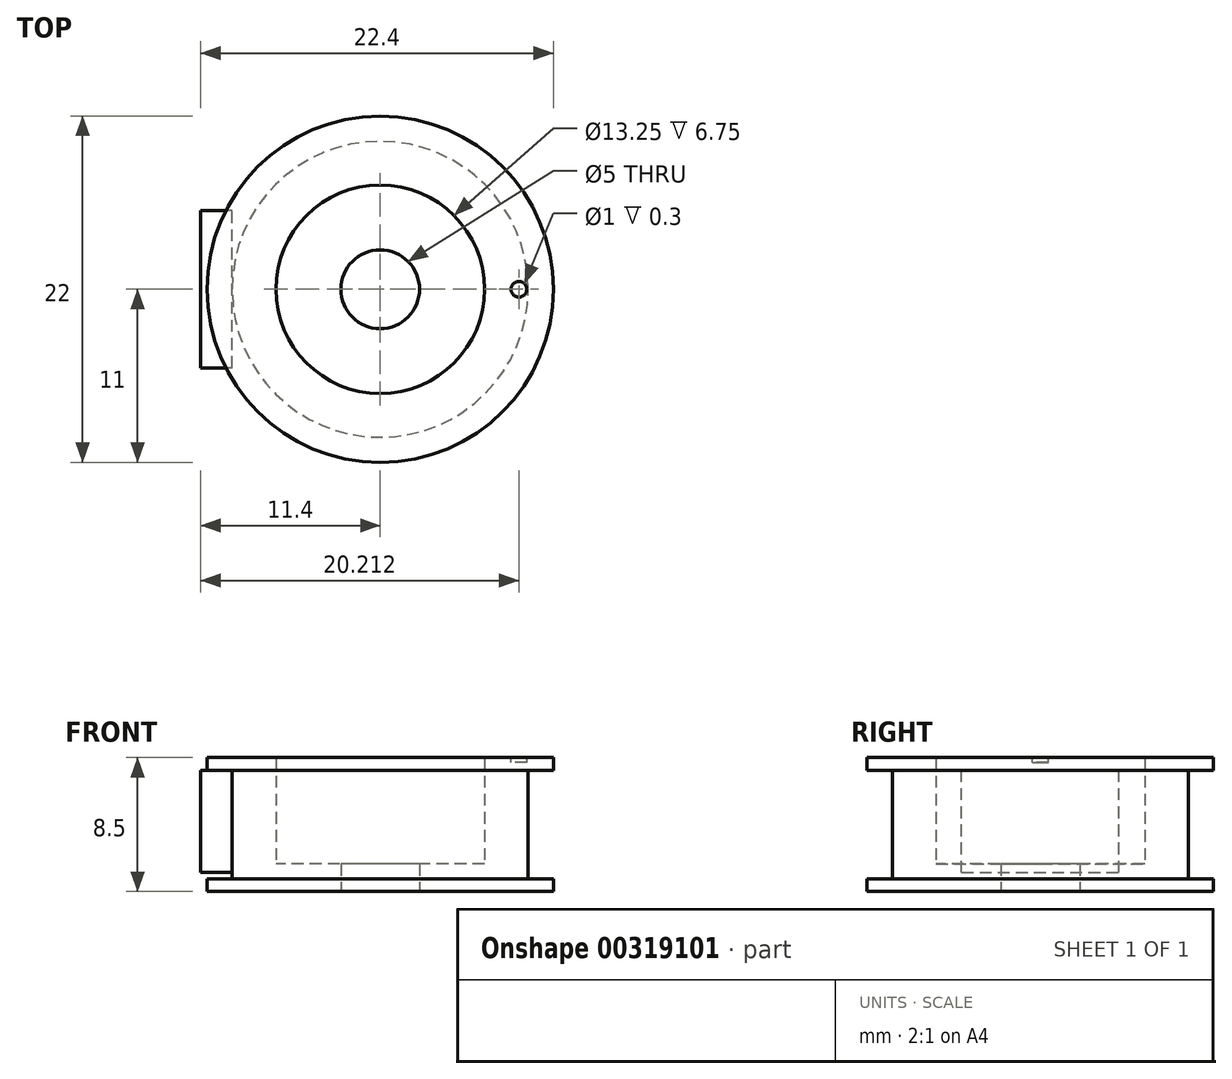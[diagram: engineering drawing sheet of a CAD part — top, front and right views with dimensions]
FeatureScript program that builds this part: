
annotation { "Feature Type Name" : "Feature", "Feature Type Description" : "" }
export const myFeature = defineFeature(function(context is Context, id is Id, definition is map)
    precondition{}
    {
        {
            assignVariable(context, id + "F0", {"name" : "Total_Height", "anyValue" : 8.5 * mm});
        }
        {
            var Q0;
            Q0=qCreatedBy(makeId("Top.planeOp"),FACE);
            var sketch = newSketch(context, id + "F1", { "sketchPlane" : qUnion([Q0])});
            skCircle(sketch, "E0", {"center": v(0, 0) * mm, "radius": 6.62 * mm});
            skCircle(sketch, "E1", {"center": v(0, 0) * mm, "radius": 11 * mm});
            skSolve(sketch);
        }
        {
            var Q0;
            Q0=makeQuery(id+"F1.imprint","IMPRINT",FACE,{"disambiguationData":[TD([[makeQuery(id+"F1.imprint","IMPRINT",EDGE,{"derivedFrom":sQuery(id+"F1.wireOp",EDGE,"E0")}),-1.0]])]});
            extrude(context, id + "F2", {"entities" : qUnion([Q0]), "depth" : getVariable(context, 'Total_Height')});
        }
        {
            var Q0;
            Q0=qCreatedBy(makeId("Top.planeOp"),FACE);
            var sketch = newSketch(context, id + "F3", { "sketchPlane" : qUnion([Q0])});
            skCircle(sketch, "E2", {"center": v(0, 0) * mm, "radius": 6.62 * mm});
            skCircle(sketch, "E3", {"center": v(0, 0) * mm, "radius": 2.5 * mm});
            skSolve(sketch);
        }
        {
            assignVariable(context, id + "F4", {"name" : "Bearing624_Height", "anyValue" : 5 * mm});
        }
        {
            var Q0;
            Q0=makeQuery(id+"F3.imprint","IMPRINT",FACE,{"disambiguationData":[TD([[makeQuery(id+"F3.imprint","IMPRINT",EDGE,{"derivedFrom":sQuery(id+"F3.wireOp",EDGE,"E2")}),1.0]])]});
            extrude(context, id + "F5", {"entities" : qUnion([Q0]), "operationType" : NewBodyOperationType.ADD, "depth" : (getVariable(context, 'Total_Height') / 2 - getVariable(context, 'Bearing624_Height') / 2)});
        }
        {
            assignVariable(context, id + "F6", {"name" : "Belt_Width", "anyValue" : 6 * mm});
        }
        {
            assignVariable(context, id + "F7", {"name" : "Extra_Belt_Width", "anyValue" : getVariable(context, 'Belt_Width') * 0.15});
        }
        {
            var Q0;
            Q0=qCreatedBy(makeId("Top.planeOp"),FACE);
            cPlane(context, id + "F8", {"entities" : qUnion([Q0]), "cplaneType" : CPlaneType.OFFSET, "offset" : (getVariable(context, 'Total_Height') / 2 - getVariable(context, 'Belt_Width') / 2 - getVariable(context, 'Extra_Belt_Width') / 2), "width" : 150 * mm, "height" : 150 * mm});
        }
        {
            var Q0;
            Q0=qCreatedBy(id+"F8.planeOp",FACE);
            var sketch = newSketch(context, id + "F9", { "sketchPlane" : qUnion([Q0])});
            skCircle(sketch, "E4", {"center": v(0, 0) * mm, "radius": 6.62 * mm, "construction": true});
            skCircle(sketch, "E5", {"center": v(0, 0) * mm, "radius": 9.4 * mm});
            skCircle(sketch, "E6", {"center": v(0, 0) * mm, "radius": 11 * mm});
            skSolve(sketch);
        }
        {
            var Q0;
            Q0 = qSketchRegion(id + "F9", true);
            extrude(context, id + "F10", {"entities" : qUnion([Q0]), "operationType" : NewBodyOperationType.REMOVE, "depth" : getVariable(context, 'Belt_Width') + getVariable(context, 'Extra_Belt_Width')});
        }
        {
            var Q0;
            Q0=makeQuery(id+"F2.opExtrude","CAP_FACE",FACE,{"disambiguationData":[OSD([sQuery(id+"F1.wireOp",EDGE,"E0"),sQuery(id+"F1.wireOp",EDGE,"E1")])],"isStart":false});
            var sketch = newSketch(context, id + "F11", { "sketchPlane" : qUnion([Q0])});
            skCircle(sketch, "E7", {"center": v(8.81, 0) * mm, "radius": 0.5 * mm});
            skPoint(sketch, "E8.0", {"position": v(0, 0) * mm});
            skSolve(sketch);
        }
        {
            var Q0;
            Q0=makeQuery(id+"F11.imprint","IMPRINT",FACE,{"disambiguationData":[TD([[makeQuery(id+"F11.imprint","IMPRINT",EDGE,{"derivedFrom":sQuery(id+"F11.wireOp",EDGE,"E7")}),1.0]])]});
            extrude(context, id + "F12", {"entities" : qUnion([Q0]), "operationType" : NewBodyOperationType.REMOVE, "oppositeDirection" : true, "depth" : 0.3 * mm});
        }
        {
            var Q0;
            Q0=qCreatedBy(makeId("Front.planeOp"),FACE);
            var sketch = newSketch(context, id + "F13", { "sketchPlane" : qUnion([Q0])});
            skLineSegment(sketch, "E9", {"start": v(-9.4, 1.2) * mm, "end": v(-9.4, 7.7) * mm});
            skLineSegment(sketch, "E10.bottom", {"start": v(-9.4, 7.7) * mm, "end": v(-11.4, 7.7) * mm});
            skLineSegment(sketch, "E10.top", {"start": v(-9.4, 1.2) * mm, "end": v(-11.4, 1.2) * mm});
            skLineSegment(sketch, "E10.left", {"start": v(-9.4, 7.7) * mm, "end": v(-9.4, 1.2) * mm});
            skLineSegment(sketch, "E10.right", {"start": v(-11.4, 7.7) * mm, "end": v(-11.4, 1.2) * mm});
            skSolve(sketch);
        }
        {
            var Q0;
            Q0=makeQuery(id+"F13.imprint","IMPRINT",FACE,{"disambiguationData":[TD([[makeQuery(id+"F13.imprint","IMPRINT",EDGE,{"derivedFrom":sQuery(id+"F13.wireOp",EDGE,"E10.bottom")}),1.0]])]});
            extrude(context, id + "F14", {"entities" : qUnion([Q0]), "endBound" : BoundingType.SYMMETRIC, "depth" : 10 * mm});
        }
    });
